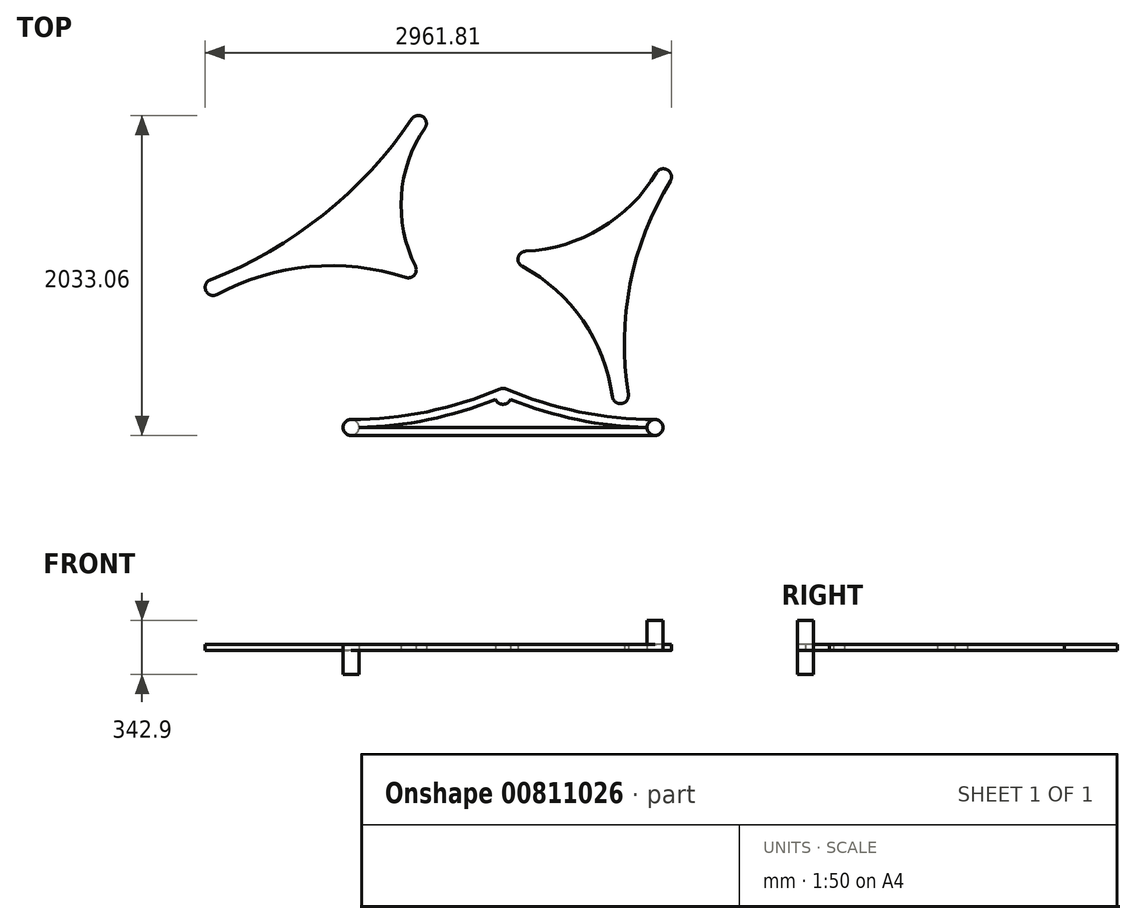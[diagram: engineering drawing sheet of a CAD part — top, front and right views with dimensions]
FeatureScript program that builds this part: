
annotation { "Feature Type Name" : "Feature", "Feature Type Description" : "" }
export const myFeature = defineFeature(function(context is Context, id is Id, definition is map)
    precondition{}
    {
        {
            var Q0;
            Q0=qCreatedBy(makeId("Top.planeOp"),FACE);
            var sketch = newSketch(context, id + "F0", { "sketchPlane" : qUnion([Q0])});
            skLineSegment(sketch, "E0", {"start": v(-335.81, -487.4) * mm, "end": v(578.59, -487.4) * mm});
            skLineSegment(sketch, "E1", {"start": v(578.59, -487.4) * mm, "end": v(578.59, -289.27) * mm, "construction": true});
            skLineSegment(sketch, "E2", {"start": v(1492.99, -487.4) * mm, "end": v(578.59, -487.4) * mm});
            skLineSegment(sketch, "E3", {"start": v(-386.61, -487.4) * mm, "end": v(-520.6, -487.4) * mm, "construction": true});
            skArc(sketch, "E4", {"start": v(-335.82, -486.86) * mm, "mid": v(106.05, -437.35) * mm, "end": v(531.69, -308.8) * mm});
            skLineSegment(sketch, "E5", {"start": v(1543.79, -487.4) * mm, "end": v(1646.2, -487.4) * mm, "construction": true});
            skArc(sketch, "E6", {"start": v(1492.99, -486.86) * mm, "mid": v(1051.12, -437.35) * mm, "end": v(625.48, -308.8) * mm});
            skArc(sketch, "E7", {"start": v(531.69, -308.8) * mm, "mid": v(578.59, -340.07) * mm, "end": v(625.48, -308.8) * mm});
            skArc(sketch, "E8", {"start": v(1543.79, -538.2) * mm, "mid": v(1594.59, -487.4) * mm, "end": v(1543.79, -436.6) * mm});
            skArc(sketch, "E9", {"start": v(-386.61, -436.6) * mm, "mid": v(-437.41, -487.4) * mm, "end": v(-386.61, -538.2) * mm});
            skArc(sketch, "E10.0", {"start": v(1543.79, -436.6) * mm, "mid": v(1061.34, -387.59) * mm, "end": v(598.6, -242.58) * mm});
            skLineSegment(sketch, "E11.0", {"start": v(1543.79, -538.2) * mm, "end": v(578.59, -538.2) * mm});
            skLineSegment(sketch, "E11.1", {"start": v(-386.61, -538.2) * mm, "end": v(578.59, -538.2) * mm});
            skArc(sketch, "E12.0", {"start": v(-386.61, -436.6) * mm, "mid": v(95.83, -387.59) * mm, "end": v(558.57, -242.58) * mm});
            skArc(sketch, "E13.trimOffspring", {"start": v(598.6, -242.58) * mm, "mid": v(578.59, -238.47) * mm, "end": v(558.57, -242.58) * mm});
            skArc(sketch, "E14.trimOffspring", {"start": v(1492.99, -486.86) * mm, "mid": v(1492.99, -487.13) * mm, "end": v(1492.99, -487.4) * mm});
            skArc(sketch, "E15.trimOffspring", {"start": v(-335.81, -487.4) * mm, "mid": v(-335.81, -487.13) * mm, "end": v(-335.82, -486.86) * mm});
            skLineSegment(sketch, "E16", {"start": v(-1262.17, 402.2) * mm, "end": v(41.41, 1444.07) * mm, "construction": true});
            skLineSegment(sketch, "E17", {"start": v(-22.61, 514.1) * mm, "end": v(-1262.17, 402.2) * mm, "construction": true});
            skLineSegment(sketch, "E18", {"start": v(-22.61, 514.1) * mm, "end": v(41.41, 1444.07) * mm, "construction": true});
            skArc(sketch, "E19", {"start": v(-38.23, 465.75) * mm, "mid": v(15.91, 480.98) * mm, "end": v(22.83, 536.8) * mm});
            skArc(sketch, "E20", {"start": v(83.32, 1415.35) * mm, "mid": v(70, 1486.07) * mm, "end": v(-0.67, 1472.52) * mm});
            skArc(sketch, "E21", {"start": v(-1280.64, 449.52) * mm, "mid": v(-1308.3, 380.91) * mm, "end": v(-1238.14, 357.44) * mm});
            skPoint(sketch, "E22.third.point", {"position": v(3234.6, 5410.07) * mm});
            skLineSegment(sketch, "E23.0", {"start": v(-1016.66, 500.87) * mm, "end": v(-46.52, 1276.24) * mm, "construction": true});
            skLineSegment(sketch, "E23.1", {"start": v(-94.17, 584.14) * mm, "end": v(-1016.66, 500.87) * mm, "construction": true});
            skLineSegment(sketch, "E23.2", {"start": v(-94.17, 584.14) * mm, "end": v(-46.52, 1276.24) * mm, "construction": true});
            skArc(sketch, "E24", {"start": v(83.32, 1415.35) * mm, "mid": v(-66.62, 984.32) * mm, "end": v(22.83, 536.8) * mm});
            skArc(sketch, "E25", {"start": v(-1280.64, 449.52) * mm, "mid": v(-562.8, 863.61) * mm, "end": v(-0.67, 1472.52) * mm});
            skArc(sketch, "E26.trimOffspring", {"start": v(-38.23, 465.75) * mm, "mid": v(-649.24, 534.04) * mm, "end": v(-1238.14, 357.44) * mm});
            skLineSegment(sketch, "E27", {"start": v(724.48, 581.55) * mm, "end": v(1598.04, 1105.3) * mm, "construction": true});
            skLineSegment(sketch, "E28", {"start": v(1324.2, -285.3) * mm, "end": v(724.48, 581.55) * mm, "construction": true});
            skLineSegment(sketch, "E29", {"start": v(1324.2, -285.3) * mm, "end": v(1598.04, 1105.3) * mm, "construction": true});
            skArc(sketch, "E30", {"start": v(1273.85, -292.01) * mm, "mid": v(1331.61, -335.57) * mm, "end": v(1374.36, -277.2) * mm});
            skArc(sketch, "E31", {"start": v(1641.37, 1078.8) * mm, "mid": v(1624.4, 1148.73) * mm, "end": v(1554.52, 1131.5) * mm});
            skArc(sketch, "E32", {"start": v(721.87, 632.29) * mm, "mid": v(674.91, 592.67) * mm, "end": v(700.45, 536.8) * mm});
            skLineSegment(sketch, "E33.0", {"start": v(833.42, 558.02) * mm, "end": v(1490.14, 951.77) * mm, "construction": true});
            skLineSegment(sketch, "E33.1", {"start": v(1284.28, -93.67) * mm, "end": v(833.42, 558.02) * mm, "construction": true});
            skLineSegment(sketch, "E33.2", {"start": v(1284.28, -93.67) * mm, "end": v(1490.14, 951.77) * mm, "construction": true});
            skArc(sketch, "E34", {"start": v(1641.37, 1078.8) * mm, "mid": v(1386.36, 424.72) * mm, "end": v(1374.36, -277.2) * mm});
            skArc(sketch, "E35", {"start": v(721.87, 632.29) * mm, "mid": v(1200.44, 778.08) * mm, "end": v(1554.52, 1131.5) * mm});
            skArc(sketch, "E36.trimOffspring", {"start": v(1273.85, -292.01) * mm, "mid": v(1087, 191.48) * mm, "end": v(700.45, 536.8) * mm});
            skSolve(sketch);
        }
        {
            var Q0;
            Q0=makeQuery(id+"F0.imprint","IMPRINT",FACE,{"disambiguationData":[TD([[makeQuery(id+"F0.imprint","IMPRINT",EDGE,{"derivedFrom":sQuery(id+"F0.wireOp",EDGE,"E0")}),-1.0]])]});
            var Q1;
            Q1=makeQuery(id+"F0.imprint","IMPRINT",FACE,{"disambiguationData":[TD([[makeQuery(id+"F0.imprint","IMPRINT",EDGE,{"derivedFrom":sQuery(id+"F0.wireOp",EDGE,"E30")}),1.0]])]});
            var Q2;
            Q2=makeQuery(id+"F0.imprint","IMPRINT",FACE,{"disambiguationData":[TD([[makeQuery(id+"F0.imprint","IMPRINT",EDGE,{"derivedFrom":sQuery(id+"F0.wireOp",EDGE,"E19")}),1.0]])]});
            extrude(context, id + "F1", {"entities" : qUnion([Q0, Q1, Q2]), "depth" : 38.1 * mm, "offsetDistance" : 25.4 * mm});
        }
        {
            var Q0;
            Q0=makeQuery(id+"F1.opExtrude","CAP_FACE",FACE,{"disambiguationData":[OSD([sQuery(id+"F0.wireOp",EDGE,"E0"),sQuery(id+"F0.wireOp",EDGE,"E2"),sQuery(id+"F0.wireOp",EDGE,"E4"),sQuery(id+"F0.wireOp",EDGE,"E6"),sQuery(id+"F0.wireOp",EDGE,"E7"),sQuery(id+"F0.wireOp",EDGE,"E8"),sQuery(id+"F0.wireOp",EDGE,"E9"),sQuery(id+"F0.wireOp",EDGE,"E10.0"),sQuery(id+"F0.wireOp",EDGE,"E11.0"),sQuery(id+"F0.wireOp",EDGE,"E11.1"),sQuery(id+"F0.wireOp",EDGE,"E12.0"),sQuery(id+"F0.wireOp",EDGE,"E13.trimOffspring"),sQuery(id+"F0.wireOp",EDGE,"E14.trimOffspring"),sQuery(id+"F0.wireOp",EDGE,"E15.trimOffspring")])],"isStart":false});
            var sketch = newSketch(context, id + "F2", { "sketchPlane" : qUnion([Q0])});
            skCircle(sketch, "E37", {"center": v(1543.79, -487.4) * mm, "radius": 50.8 * mm});
            skSolve(sketch);
        }
        {
            var Q0;
            {var subQ0=sQuery(id+"F2.wireOp",EDGE,"E37");var subQ4=makeQuery(id+"F2.imprint","INTERSECT",VERTEX,{"derivedFrom":[makeQuery(id+"F1.opExtrude","CAP_EDGE",EDGE,{"disambiguationData":[OSD([sQuery(id+"F0.wireOp",EDGE,"E6")])],"isStart":false}),subQ0]});Q0=makeQuery(id+"F2.imprint","IMPRINT",FACE,{"disambiguationData":[TD([[makeQuery(id+"F2.imprint","IMPRINT",EDGE,{"disambiguationData":[TD([[subQ4,1.0]])],"derivedFrom":subQ0}),1.0]])]});}
            extrude(context, id + "F3", {"entities" : qUnion([Q0]), "operationType" : NewBodyOperationType.ADD, "depth" : 152.4 * mm, "offsetDistance" : 25.4 * mm});
        }
        {
            var Q0;
            Q0=makeQuery(id+"F1.opExtrude","CAP_FACE",FACE,{"disambiguationData":[OSD([sQuery(id+"F0.wireOp",EDGE,"E0"),sQuery(id+"F0.wireOp",EDGE,"E2"),sQuery(id+"F0.wireOp",EDGE,"E4"),sQuery(id+"F0.wireOp",EDGE,"E6"),sQuery(id+"F0.wireOp",EDGE,"E7"),sQuery(id+"F0.wireOp",EDGE,"E8"),sQuery(id+"F0.wireOp",EDGE,"E9"),sQuery(id+"F0.wireOp",EDGE,"E10.0"),sQuery(id+"F0.wireOp",EDGE,"E11.0"),sQuery(id+"F0.wireOp",EDGE,"E11.1"),sQuery(id+"F0.wireOp",EDGE,"E12.0"),sQuery(id+"F0.wireOp",EDGE,"E13.trimOffspring"),sQuery(id+"F0.wireOp",EDGE,"E14.trimOffspring"),sQuery(id+"F0.wireOp",EDGE,"E15.trimOffspring")])],"isStart":true});
            var sketch = newSketch(context, id + "F4", { "sketchPlane" : qUnion([Q0])});
            skCircle(sketch, "E38", {"center": v(-386.61, 487.4) * mm, "radius": 50.8 * mm});
            skSolve(sketch);
        }
        {
            var Q0;
            {var subQ0=sQuery(id+"F4.wireOp",EDGE,"E38");var subQ1=makeQuery(id+"F4.imprint","INTERSECT",VERTEX,{"derivedFrom":[makeQuery(id+"F1.opExtrude","CAP_EDGE",EDGE,{"disambiguationData":[OSD([sQuery(id+"F0.wireOp",EDGE,"E12.0")])],"isStart":true}),subQ0]});var subQ4=makeQuery(id+"F4.imprint","INTERSECT",VERTEX,{"derivedFrom":[makeQuery(id+"F1.opExtrude","CAP_EDGE",EDGE,{"disambiguationData":[OSD([sQuery(id+"F0.wireOp",EDGE,"E4")])],"isStart":true}),subQ0]});Q0=makeQuery(id+"F4.imprint","IMPRINT",FACE,{"disambiguationData":[TD([[makeQuery(id+"F4.imprint","IMPRINT",EDGE,{"disambiguationData":[TD([[subQ4,1.0],[subQ1,-1.0]])],"derivedFrom":subQ0}),1.0]])]});}
            extrude(context, id + "F5", {"entities" : qUnion([Q0]), "operationType" : NewBodyOperationType.ADD, "depth" : 152.4 * mm, "offsetDistance" : 25.4 * mm});
        }
    });
